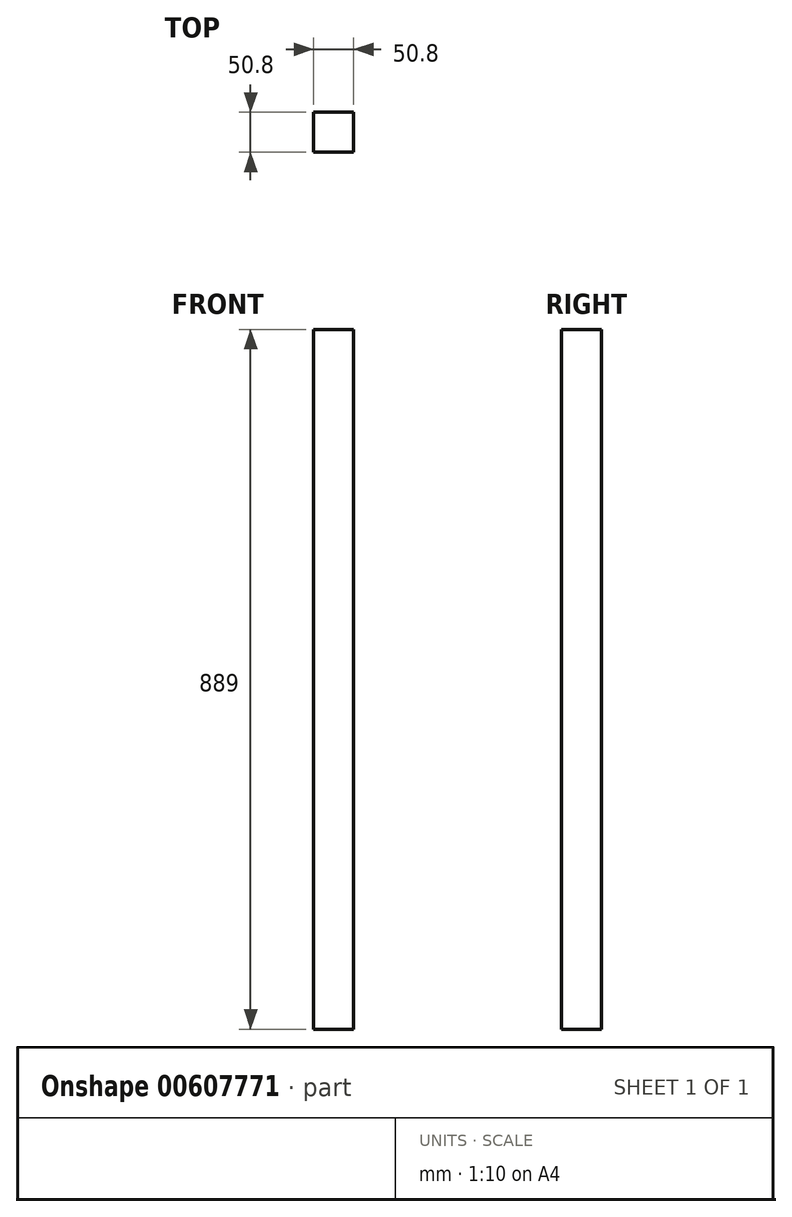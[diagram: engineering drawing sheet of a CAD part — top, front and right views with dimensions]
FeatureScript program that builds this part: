
annotation { "Feature Type Name" : "Feature", "Feature Type Description" : "" }
export const myFeature = defineFeature(function(context is Context, id is Id, definition is map)
    precondition{}
    {
        {
            var Q0;
            Q0=qCreatedBy(makeId("Top.planeOp"),FACE);
            var sketch = newSketch(context, id + "F0", { "sketchPlane" : qUnion([Q0])});
            skLineSegment(sketch, "E0.bottom", {"start": v(25.4, 25.4) * mm, "end": v(-25.4, 25.4) * mm});
            skLineSegment(sketch, "E0.top", {"start": v(25.4, -25.4) * mm, "end": v(-25.4, -25.4) * mm});
            skLineSegment(sketch, "E0.left", {"start": v(25.4, 25.4) * mm, "end": v(25.4, -25.4) * mm});
            skLineSegment(sketch, "E0.right", {"start": v(-25.4, 25.4) * mm, "end": v(-25.4, -25.4) * mm});
            skPoint(sketch, "E0.middle", {"position": v(0, 0) * mm});
            skSolve(sketch);
        }
        {
            var Q0;
            Q0=makeQuery(id+"F0.imprint","IMPRINT",FACE,{"disambiguationData":[TD([[makeQuery(id+"F0.imprint","IMPRINT",EDGE,{"derivedFrom":sQuery(id+"F0.wireOp",EDGE,"E0.bottom")}),1.0]])]});
            extrude(context, id + "F1", {"entities" : qUnion([Q0]), "depth" : 889 * mm, "offsetDistance" : 25.4 * mm});
        }
    });
